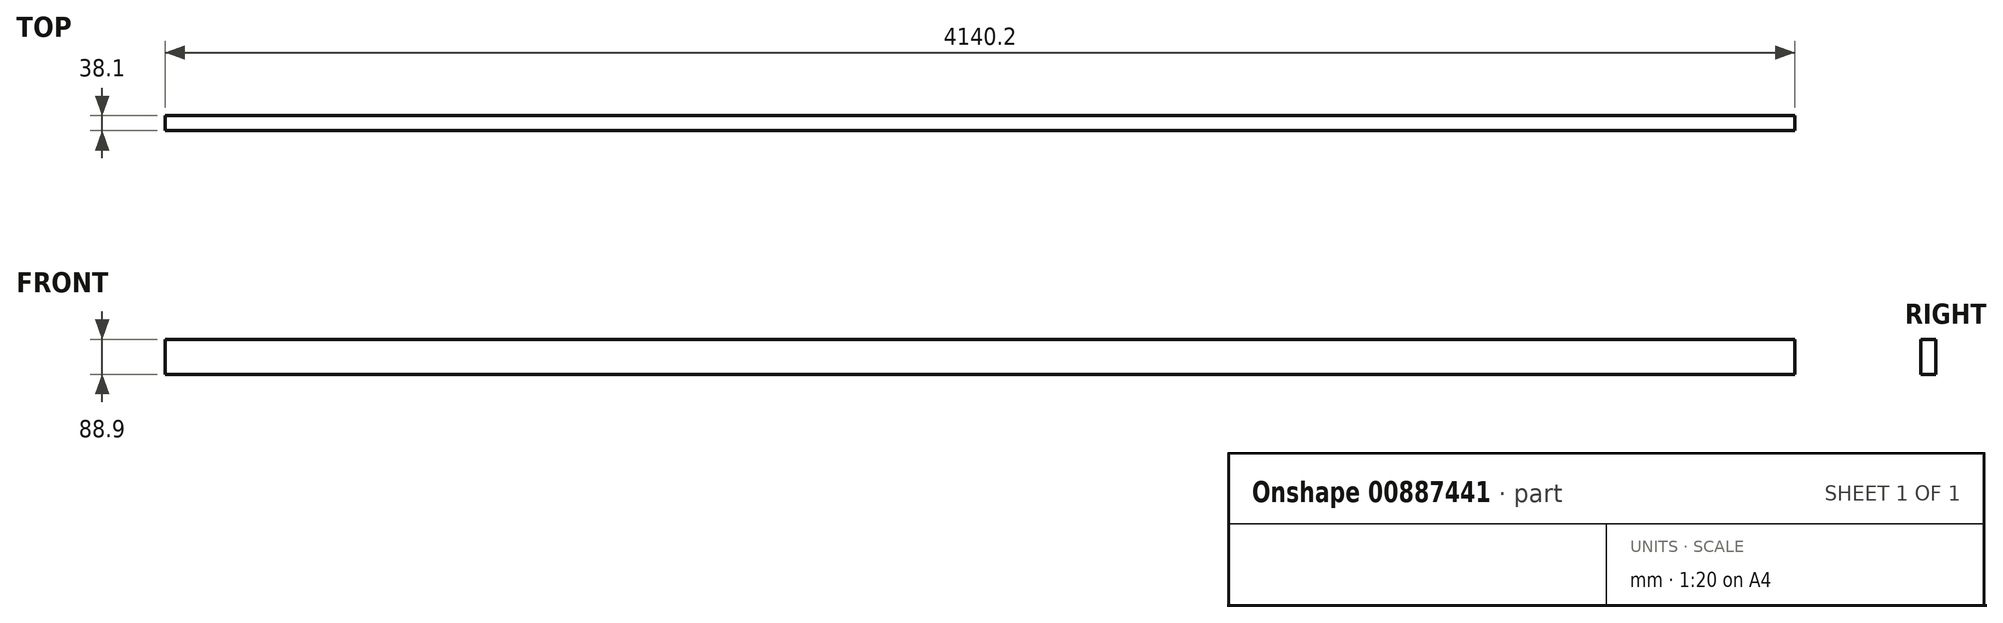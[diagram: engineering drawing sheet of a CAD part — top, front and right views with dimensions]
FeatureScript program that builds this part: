
annotation { "Feature Type Name" : "Feature", "Feature Type Description" : "" }
export const myFeature = defineFeature(function(context is Context, id is Id, definition is map)
    precondition{}
    {
        {
            var Q0;
            Q0=qCreatedBy(makeId("Top.planeOp"),FACE);
            var sketch = newSketch(context, id + "F0", { "sketchPlane" : qUnion([Q0])});
            skLineSegment(sketch, "E0.bottom", {"start": v(2070.1, 19.05) * mm, "end": v(-2070.1, 19.05) * mm});
            skLineSegment(sketch, "E0.top", {"start": v(2070.1, -19.05) * mm, "end": v(-2070.1, -19.05) * mm});
            skLineSegment(sketch, "E0.left", {"start": v(2070.1, 19.05) * mm, "end": v(2070.1, -19.05) * mm});
            skLineSegment(sketch, "E0.right", {"start": v(-2070.1, 19.05) * mm, "end": v(-2070.1, -19.05) * mm});
            skPoint(sketch, "E0.middle", {"position": v(0, 0) * mm});
            skSolve(sketch);
        }
        {
            var Q0;
            Q0=makeQuery(id+"F0.imprint","IMPRINT",FACE,{"disambiguationData":[TD([[makeQuery(id+"F0.imprint","IMPRINT",EDGE,{"derivedFrom":sQuery(id+"F0.wireOp",EDGE,"E0.bottom")}),1.0]])]});
            extrude(context, id + "F1", {"entities" : qUnion([Q0]), "depth" : 88.9 * mm, "offsetDistance" : 25.4 * mm});
        }
    });
